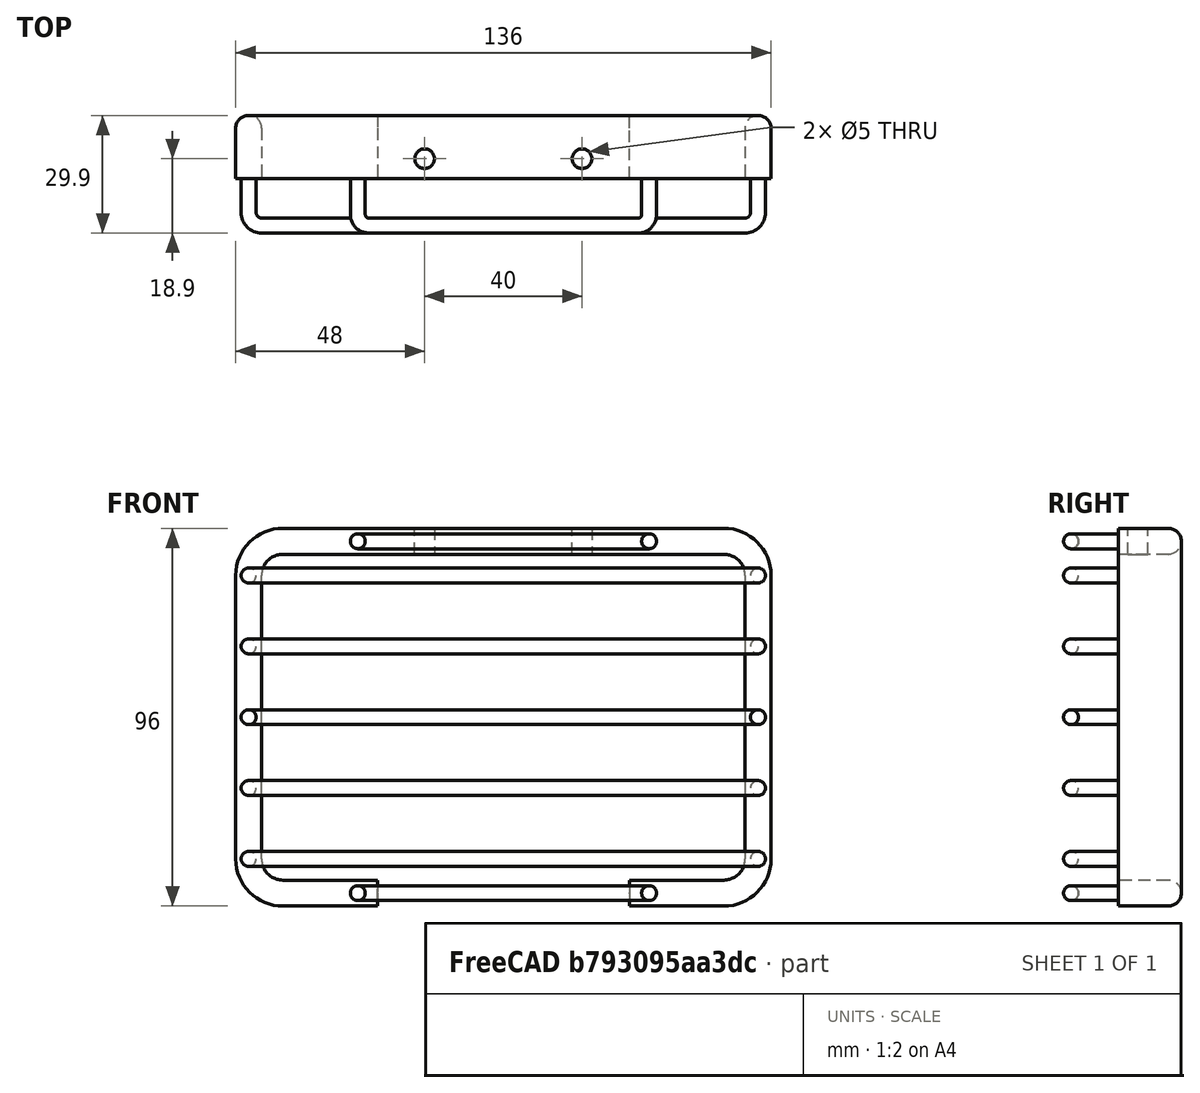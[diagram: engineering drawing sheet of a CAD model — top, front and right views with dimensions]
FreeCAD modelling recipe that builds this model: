
FCSTD DOCUMENT  (FreeCAD 0.21R33771 (Git))
Label: ex25
License: All rights reserved
LicenseURL: https://en.wikipedia.org/wiki/All_rights_reserved
objects: Sketcher::SketchObject×7, PartDesign::Pocket×2, PartDesign::AdditivePipe×2, PartDesign::LinearPattern×2, PartDesign::Pad×1, PartDesign::Thickness×1, PartDesign::Fillet×1, PartDesign::Mirrored×1, PartDesign::Body×1
note: 25 computed .brp shape members not serialized (recipe doc carries the construction recipe); baked Part::Feature solids carry a one-line shape summary decoded from their .brp

FEATURE [Sketcher::SketchObject] Sketch
  FullyConstrained = true
  MapMode = 5
  Placement = pos=(0,0,0) rot=(1,0,0;1.5708rad)
  Support = -> [XZ_Plane]
  sketch-geometry (10):
    g0: ArcOfCircle CenterX=-56 CenterY=36 CenterZ=0 NormalX=0 NormalY=0 NormalZ=1 AngleXU=0 Radius=12 StartAngle=1.5708 EndAngle=3.14159
    g1: LineSegment StartX=-56 StartY=48 StartZ=0 EndX=56 EndY=48 EndZ=0
    g2: ArcOfCircle CenterX=56 CenterY=36 CenterZ=0 NormalX=0 NormalY=0 NormalZ=1 AngleXU=0 Radius=12 StartAngle=-8e-15 EndAngle=1.5708
    g3: LineSegment StartX=68 StartY=36 StartZ=0 EndX=68 EndY=-36 EndZ=0
    g4: ArcOfCircle CenterX=56 CenterY=-36 CenterZ=0 NormalX=0 NormalY=0 NormalZ=1 AngleXU=0 Radius=12 StartAngle=4.71239 EndAngle=6.28319
    g5: LineSegment StartX=56 StartY=-48 StartZ=0 EndX=-56 EndY=-48 EndZ=0
    g6: ArcOfCircle CenterX=-56 CenterY=-36 CenterZ=0 NormalX=0 NormalY=0 NormalZ=1 AngleXU=0 Radius=12 StartAngle=3.14159 EndAngle=4.71239
    g7: LineSegment StartX=-68 StartY=-36 StartZ=0 EndX=-68 EndY=36 EndZ=0
    g8: GeomPoint X=-68 Y=48 Z=0
    g9: GeomPoint X=68 Y=-48 Z=0
  constraints (22):
    c: Tangent(g0,g1) = 1.5708
    c: Tangent(g1,g2) = 1.5708
    c: Tangent(g2,g3) = 1.5708
    c: Tangent(g3,g4) = 1.5708
    c: Tangent(g4,g5) = 1.5708
    c: Tangent(g5,g6) = 1.5708
    c: Tangent(g6,g7) = 1.5708
    c: Tangent(g7,g0) = 1.5708
    c: Horizontal(g1)
    c: Horizontal(g5)
    c: Vertical(g3)
    c: Vertical(g7)
    c: Equal(g2,g4)
    c: PointOnObject(g8,g1)
    c: PointOnObject(g8,g7)
    c: PointOnObject(g9,g3)
    c: PointOnObject(g9,g5)
    c: Symmetric(g2,g0,g-2)
    c: Symmetric(g6,g0,g-1)
    c: Radius(g0) = 12
    c: DistanceX(g0,g2) = 136
    c: DistanceY(g4,g1) = 96
FEATURE [PartDesign::Pad] Pad
  Direction = (0,-1,2e-16)
  Length = 16
  Length2 = 10
  Placement = pos=(0,0,0) rot=(1,0,0;1.5708rad)
  Profile = -> Sketch
  ReferenceAxis = -> Sketch [N_Axis]
  Type = 0
FEATURE [PartDesign::Thickness] Thickness
  Base = -> Pad [Face10,Face9]
  BaseFeature = -> Pad
  Intersection = false
  Join = 0
  Mode = 0
  Reversed = true
  SupportTransform = false
  Value = 6.6
FEATURE [PartDesign::Fillet] Fillet
  Base = -> Thickness [Edge40,Edge39,Edge12,Edge9]
  BaseFeature = -> Thickness
  Radius = 3.29
  SupportTransform = false
  UseAllEdges = false
FEATURE [Sketcher::SketchObject] Sketch001
  ExternalGeometry = -> [Fillet]
  FullyConstrained = true
  MapMode = 5
  Placement = pos=(0,1.07e-14,48) rot=(0,0,1;0rad)
  Support = -> [Fillet]
  sketch-geometry (2):
    g0: Circle CenterX=-20 CenterY=-11 CenterZ=0 NormalX=0 NormalY=0 NormalZ=1 AngleXU=0 Radius=2.5
    g1: Circle CenterX=20 CenterY=-11 CenterZ=0 NormalX=0 NormalY=0 NormalZ=1 AngleXU=0 Radius=2.5
  constraints (5):
    c: Equal(g1,g0)
    c: Symmetric(g0,g1,g-2)
    c: Radius(g0) = 2.5
    c: DistanceX(g0,g1) = 40
    c: Distance(g1,g-3) = 5
FEATURE [PartDesign::Pocket] Pocket
  BaseFeature = -> Fillet
  Direction = (0,-2e-16,-1)
  Length = 10
  Length2 = 5
  Profile = -> Sketch001
  ReferenceAxis = -> Sketch001 [N_Axis]
  Type = 0
FEATURE [Sketcher::SketchObject] Sketch002
  ExternalGeometry = -> [Pocket]
  FullyConstrained = false
  MapMode = 5
  Support = -> [XY_Plane]
  sketch-geometry (5):
    g0: LineSegment StartX=64.7 StartY=-16 StartZ=0 EndX=64.7 EndY=-24.6551 EndZ=0
    g1: LineSegment StartX=61.3551 StartY=-28 StartZ=0 EndX=-61.3551 EndY=-28 EndZ=0
    g2: LineSegment StartX=-64.7 StartY=-24.6551 StartZ=0 EndX=-64.7 EndY=-16 EndZ=0
    g3: ArcOfCircle CenterX=-61.3551 CenterY=-24.6551 CenterZ=0 NormalX=0 NormalY=0 NormalZ=1 AngleXU=0 Radius=3.3449 StartAngle=3.14159 EndAngle=4.71239
    g4: ArcOfCircle CenterX=61.3551 CenterY=-24.6551 CenterZ=0 NormalX=0 NormalY=0 NormalZ=1 AngleXU=0 Radius=3.3449 StartAngle=4.71239 EndAngle=6.28319
  constraints (11):
    c: Horizontal(g1)
    c: Vertical(g0)
    c: Vertical(g2)
    c: PointOnObject(g2,g-4)
    c: Tangent(g2,g3) = 1.5708
    c: Tangent(g1,g3) = 1.5708
    c: Tangent(g0,g4) = 1.5708
    c: Tangent(g1,g4) = 1.5708
    c: DistanceX(g2,g0) = 129.4
    c: Symmetric(g2,g0,g-2)
    c: DistanceY(g1,g-5) = 12
FEATURE [Sketcher::SketchObject] Sketch003
  ExternalGeometry = -> [Sketch002]
  FullyConstrained = true
  MapMode = 5
  Placement = pos=(0,-16,3.6e-15) rot=(1,0,0;1.5708rad)
  Support = -> [Pocket]
  sketch-geometry (1):
    g0: Circle CenterX=64.7 CenterY=0 CenterZ=0 NormalX=0 NormalY=0 NormalZ=1 AngleXU=0 Radius=1.9
  constraints (2):
    c: Coincident(g0,g-3)
    c: Radius(g0) = 1.9
FEATURE [PartDesign::AdditivePipe] AdditivePipe
  AuxilleryCurvelinear = true
  AuxillerySpineTangent = false
  BaseFeature = -> Pocket
  Binormal = (0,0,0)
  Mode = 0
  Profile = -> Sketch003
  Spine = -> Sketch002
  SpineTangent = false
  Transformation = 0
  Transition = 0
FEATURE [PartDesign::LinearPattern] LinearPattern
  BaseFeature = -> AdditivePipe
  Direction = -> Z_Axis
  Length = 36
  Occurrences = 3
  Originals = -> [AdditivePipe]
  Reversed = true
FEATURE [PartDesign::LinearPattern] LinearPattern001
  BaseFeature = -> LinearPattern
  Direction = -> Z_Axis
  Length = 36
  Occurrences = 3
  Originals = -> [AdditivePipe]
FEATURE [Sketcher::SketchObject] Sketch004
  FullyConstrained = false
  MapMode = 5
  Placement = pos=(0,-16,3.6e-15) rot=(1,0,0;1.5708rad)
  Support = -> [LinearPattern001]
  sketch-geometry (5):
    g0: LineSegment StartX=-32 StartY=-51.5558 StartZ=0 EndX=-32 EndY=-39.4519 EndZ=0
    g1: LineSegment StartX=-32 StartY=-39.4519 StartZ=0 EndX=32 EndY=-39.4519 EndZ=0
    g2: LineSegment StartX=32 StartY=-39.4519 StartZ=0 EndX=32 EndY=-51.5558 EndZ=0
    g3: LineSegment StartX=32 StartY=-51.5558 StartZ=0 EndX=-32 EndY=-51.5558 EndZ=0
    g4: GeomPoint X=-2.3e-15 Y=-45.5039 Z=0
  constraints (10):
    c: Coincident(g0,g1)
    c: Coincident(g1,g2)
    c: Coincident(g2,g3)
    c: Coincident(g3,g0)
    c: Horizontal(g1)
    c: Vertical(g0)
    c: Vertical(g2)
    c: Symmetric(g1,g0,g4)
    c: Symmetric(g2,g0,g-2)
    c: DistanceX(g3,g3) = 64
FEATURE [PartDesign::Pocket] Pocket001
  BaseFeature = -> LinearPattern001
  Direction = (0,1,-2e-16)
  Length = 17
  Length2 = 5
  Profile = -> Sketch004
  ReferenceAxis = -> Sketch004 [N_Axis]
  Type = 0
FEATURE [Sketcher::SketchObject] Sketch005
  AttachmentOffset = pos=(0,0,-3.3) rot=(0,0,1;0rad)
  ExternalGeometry = -> [Pocket001]
  FullyConstrained = false
  MapMode = 5
  Placement = pos=(0,9.9e-15,44.7) rot=(0,0,1;0rad)
  Support = -> [Pocket001]
  sketch-geometry (5):
    g0: LineSegment StartX=37.0345 StartY=-15.9997 StartZ=0 EndX=37.0345 EndY=-25.2406 EndZ=0
    g1: LineSegment StartX=34.274 StartY=-27.9997 StartZ=0 EndX=-34.2078 EndY=-27.9666 EndZ=0
    g2: LineSegment StartX=-36.9655 StartY=-25.2075 StartZ=0 EndX=-36.9655 EndY=-16 EndZ=0
    g3: ArcOfCircle CenterX=-34.2065 CenterY=-25.2075 CenterZ=0 NormalX=0 NormalY=0 NormalZ=1 AngleXU=0 Radius=2.75908 StartAngle=3.14159 EndAngle=4.71191
    g4: ArcOfCircle CenterX=34.2754 CenterY=-25.2406 CenterZ=0 NormalX=0 NormalY=0 NormalZ=1 AngleXU=0 Radius=2.75908 StartAngle=4.71191 EndAngle=6.28319
  constraints (10):
    c: Vertical(g0)
    c: Vertical(g2)
    c: PointOnObject(g2,g-3)
    c: Tangent(g2,g3) = 1.5708
    c: Tangent(g1,g3) = 1.5708
    c: Tangent(g0,g4) = 1.5708
    c: Tangent(g1,g4) = 1.5708
    c: Equal(g4,g3)
    c: DistanceY(g1,g0) = 12
    c: DistanceX(g2,g0) = 74
FEATURE [Sketcher::SketchObject] Sketch006
  ExternalGeometry = -> [Sketch005]
  FullyConstrained = true
  MapMode = 5
  Placement = pos=(0,-16,3.6e-15) rot=(1,0,0;1.5708rad)
  Support = -> [Pocket001]
  sketch-geometry (1):
    g0: Circle CenterX=-36.9655 CenterY=44.7 CenterZ=0 NormalX=0 NormalY=0 NormalZ=1 AngleXU=0 Radius=1.9
  constraints (2):
    c: Coincident(g0,g-3)
    c: Radius(g0) = 1.9
FEATURE [PartDesign::AdditivePipe] AdditivePipe001
  AuxilleryCurvelinear = true
  AuxillerySpineTangent = false
  BaseFeature = -> Pocket001
  Binormal = (0,0,0)
  Mode = 0
  Profile = -> Sketch006
  Spine = -> Sketch005
  SpineTangent = false
  Transformation = 0
  Transition = 0
FEATURE [PartDesign::Mirrored] Mirrored
  BaseFeature = -> AdditivePipe001
  MirrorPlane = -> XY_Plane
  Originals = -> [AdditivePipe001]
FEATURE [PartDesign::Body] Body
  Group = -> [Sketch,Pad,Thickness,Fillet,Sketch001,Pocket,Sketch002,Sketch003,AdditivePipe,LinearPattern,LinearPattern001,Sketch004,Pocket001,Sketch005,Sketch006,AdditivePipe001,Mirrored]
  Origin = -> Origin
  Tip = -> Mirrored
